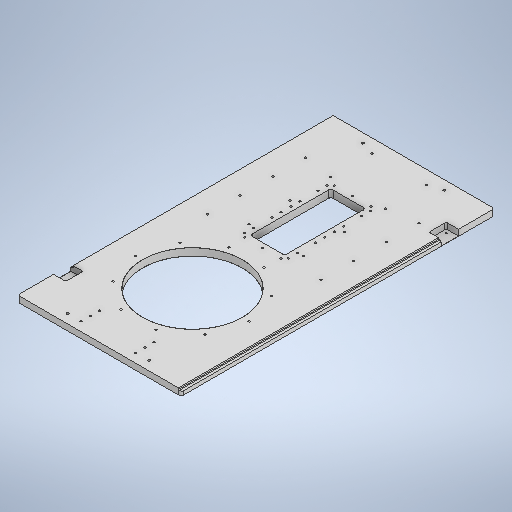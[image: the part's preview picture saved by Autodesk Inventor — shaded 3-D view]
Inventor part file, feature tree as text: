
AUTODESK INVENTOR PART (.ipt)
format: ipt  version: 2025 (Build 290162000, 162)  size: 565,760 bytes
history: native  units: in
note: dims shown in document units (in); Inventor stores cm internally (conversion verified against a paired STEP export)
features: sketch x17, extrude x6, hole x5, fillet x3, chamfer x3, plane x2
ambient origin geometry x8: Origin, YZ Plane, XZ Plane, XY Plane, X Axis, Y Axis, Z Axis, Center Point
bodies: Solid1 (feature_tree)
feature tree (36):
  extrude  "Base Cover"  Depth=27.1654in
  sketch  "Sketch2"  dims[d5=8.6614in d6=0.0in d7=0.0in]
  extrude  "Cylinder Hole"  Depth=0.6299in
  plane  "Work Plane1"
  hole  "Hole3"  [1 undecoded]
  sketch  "Sketch7"  dims[d69=0.1575in d70=3.937in d72=360.0deg]
  plane  "Work Plane2"
  hole  "Hole4"  [1 undecoded]
  sketch  "Sketch9"  dims[d82=1.063in]
  fillet  "Rounded Side Corners"  Radius=7.0625in
  chamfer  "Chamfer1"  Distance=3.937in Angle=360.0deg
  chamfer  "Chamfer2"  Distance=0.1969in
  extrude  "Magnet Seats"  Depth=0.3937in TaperAngle=45.0deg
  hole  "Hole5"  [1 undecoded]
  chamfer  "Chamfer5"  Distance=0.1181in
  hole  "Hole6"  [1 undecoded]
  sketch  "Sketch15"  dims[d85=1.4961in]
  extrude  "Extrusion11"  Depth=0.3937in TaperAngle=0.0deg
  fillet  "Fillet3"  Radius=0.748in
  hole  "Hole7"  [1 undecoded]
  fillet  "Rounded Bottom Corners"  Radius=0.8661in
  extrude  "Side Rail_L"  Depth=0.3937in
  extrude  "Side Rail_R"  Depth=0.3937in
  sketch  "Sketch1"  dims[d0=14.1732in d1=27.1654in]
  sketch  "Sketch6"  dims[d68=9.8425in]
  sketch  "Sketch8"  dims[d74=0.1628in d75=0.3937in d76=0.1575in d77=0.0787in d78=90.0deg d79=0.3937in d80=0.8108in]
  sketch  "Sketch Circular Pattern4"  dims[d57=0.1936in d58=0.1969in d59=0.1575in d60=0.0787in d61=90.0deg d62=0.1969in d63=0.8108in]
  sketch  "Sketch11"  dims[d83=1.063in]
  sketch  "Sketch12"  dims[d84=1.4961in]
  sketch  "Sketch Rectangular Pattern1"  dims[d2=0.6299in d3=0.0in d4=8.0709in]
  sketch  "Sketch Rectangular Pattern2"  dims[d8=10.6299in d50=5.9055in d55=7.0625in]
  sketch  "Sketch Rectangular Pattern3"  dims[d56=25.5906in]
  sketch  "Sketch Rectangular Pattern4"  dims[d64=10.3543in]
  sketch  "Sketch Rectangular Pattern5"  dims[d65=10.6299in]
  sketch  "Sketch16"  dims[d86=3.1102in]
  sketch  "Sketch17"  dims[d87=3.1102in d88=0.1969in d89=0.0984in d90=0.0787in d91=45.0deg d92=0.0984in d93=0.0787in d94=45.0deg d95=0.1181in d96=0.1181in d97=0.5118in d98=0.0in d109=0.748in d110=0.315in d111=0.8661in d112=0.748in d113=0.1299in d114=0.1299in d115=0.1299in d116=0.1299in d118=0.315in d119=0.8661in d120=0.748in d121=0.748in d122=0.1276in d123=0.315in d124=0.1575in d125=0.0787in d126=90.0deg d127=0.315in d128=0.8108in d129=0.0138in d130=0.0787in d131=45.0deg d146=3.9469in d147=0.7874in d148=0.3937in d149=0.1575in d150=3.937in d152=1.1811in d153=0.3937in d155=0.3937in d157=0.1575in d158=1.1811in d160=0.7874in d161=0.3937in d163=0.3937in d165=9.8425in d166=0.1575in d167=2.9528in d168=1.1811in d169=3.1496in d171=1.4173in d172=0.3937in d174=0.3937in d176=0.1628in d177=0.3937in d178=0.1575in d179=0.0787in d180=90.0deg d181=0.3937in d182=0.8108in d191=3.0in d192=7.0in d193=6.4961in d194=0.8312in d195=0.0in d196=0.1969in d197=0.3937in d198=0.1969in d199=1.9685in d201=0.7874in d202=0.3937in d204=0.3937in d206=0.3189in d207=0.1969in d208=0.3189in d209=1.9685in d211=0.7874in d212=0.3937in d214=0.3937in d216=0.1628in d217=0.3937in d218=0.1575in d219=0.0787in d220=90.0deg d221=0.3937in d222=0.8108in d230=0.2756in d231=0.2362in d232=0.0787in d233=0.1378in d234=0.503in d235=0.5906in d236=0.0in d237=0.1378in d238=0.0787in d239=0.2362in d240=0.503in d241=0.3937in d242=0.0in d26=0.0394in d27=0.0394in d28=0.0394in d29=0.0059in d30=0.0098in d31=0.0148in d32=0.5635in d33=0.0295in d34=0.8108in d35=0.0025in d36=0.0295in d37=0.0148in d66=0.0197in d67=0.0344in]
note: 5 required parameter values undecoded (feature->parameter linkage not recoverable at this tier; creation-order binding heuristic only, values carry confidence <= 0.55)
